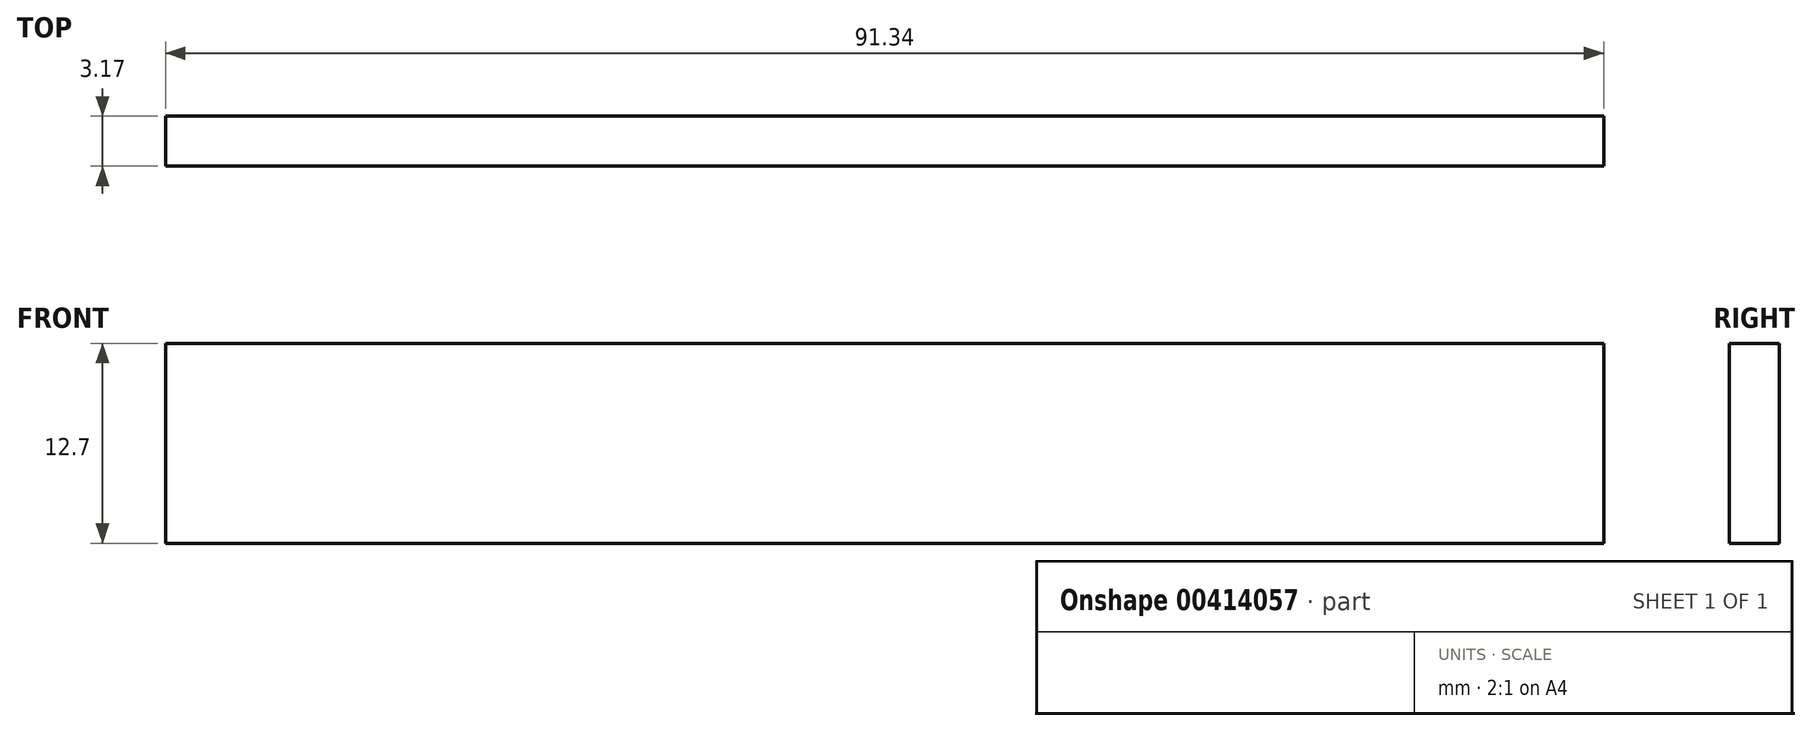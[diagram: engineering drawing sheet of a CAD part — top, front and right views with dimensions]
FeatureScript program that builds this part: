
annotation { "Feature Type Name" : "Feature", "Feature Type Description" : "" }
export const myFeature = defineFeature(function(context is Context, id is Id, definition is map)
    precondition{}
    {
        {
            var Q0;
            Q0=qCreatedBy(makeId("Front.planeOp"),FACE);
            var sketch = newSketch(context, id + "F0", { "sketchPlane" : qUnion([Q0])});
            skLineSegment(sketch, "E0.bottom", {"start": v(45.67, 6.35) * mm, "end": v(-45.67, 6.35) * mm});
            skLineSegment(sketch, "E0.top", {"start": v(45.67, -6.35) * mm, "end": v(-45.67, -6.35) * mm});
            skLineSegment(sketch, "E0.left", {"start": v(45.67, 6.35) * mm, "end": v(45.67, -6.35) * mm});
            skLineSegment(sketch, "E0.right", {"start": v(-45.67, 6.35) * mm, "end": v(-45.67, -6.35) * mm});
            skPoint(sketch, "E0.middle", {"position": v(0, 0) * mm});
            skSolve(sketch);
        }
        {
            var Q0;
            Q0=makeQuery(id+"F0.imprint","IMPRINT",FACE,{"disambiguationData":[TD([[makeQuery(id+"F0.imprint","IMPRINT",EDGE,{"derivedFrom":sQuery(id+"F0.wireOp",EDGE,"E0.bottom")}),1.0]])]});
            extrude(context, id + "F1", {"entities" : qUnion([Q0]), "depth" : 3.17 * mm});
        }
    });
